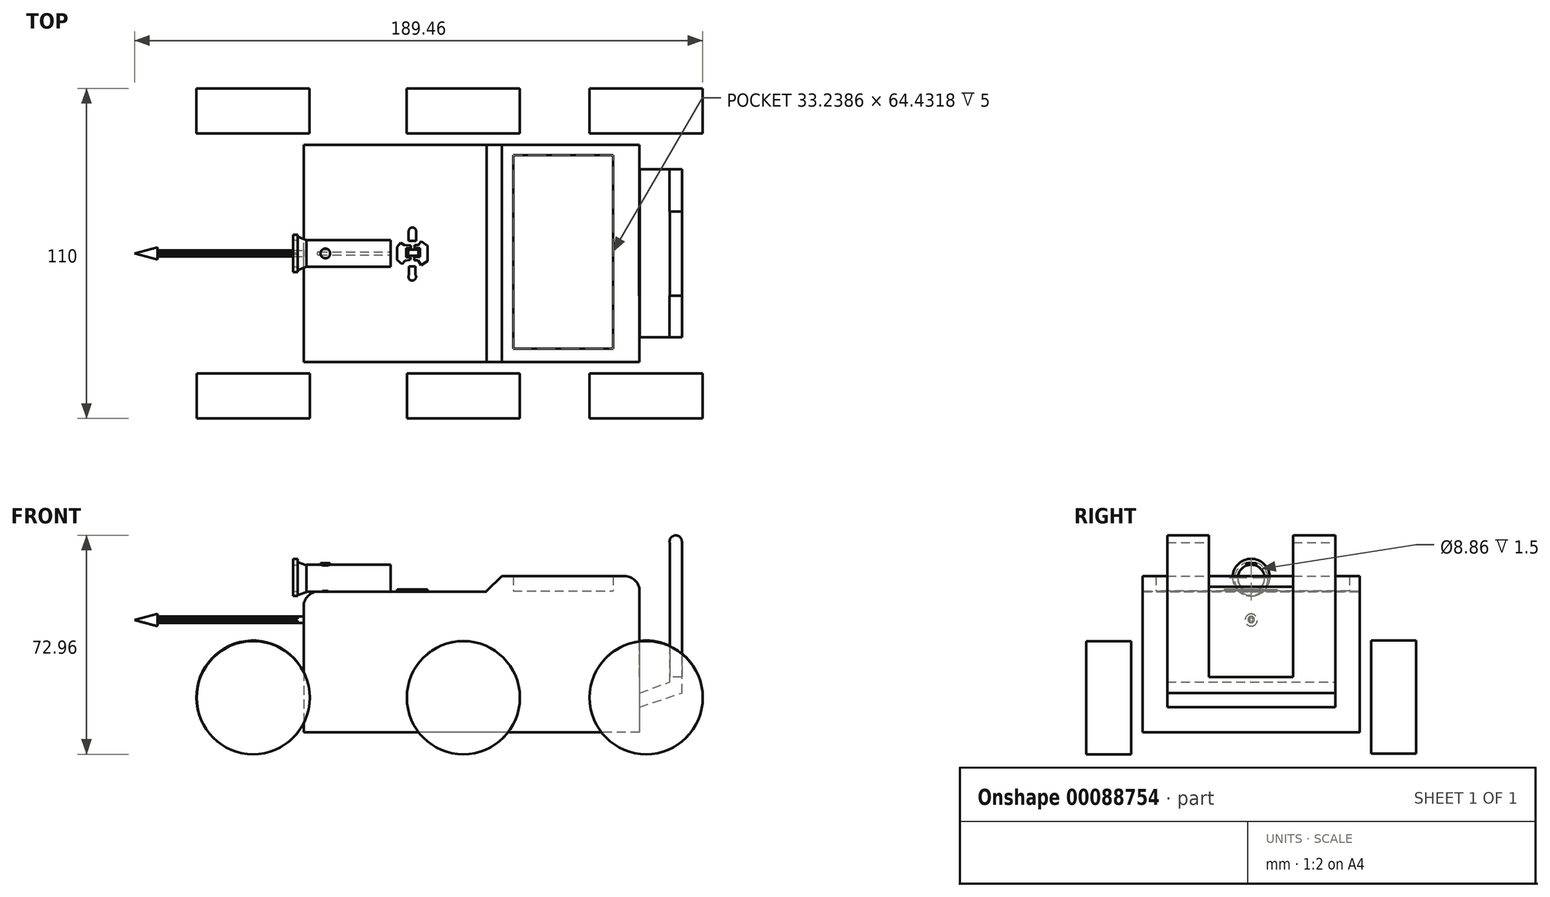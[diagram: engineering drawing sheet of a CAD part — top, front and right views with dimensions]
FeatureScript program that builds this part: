
annotation { "Feature Type Name" : "Feature", "Feature Type Description" : "" }
export const myFeature = defineFeature(function(context is Context, id is Id, definition is map)
    precondition{}
    {
        {
            var Q0;
            Q0=qCreatedBy(makeId("Front.planeOp"),FACE);
            var sketch = newSketch(context, id + "F0", { "sketchPlane" : qUnion([Q0])});
            skLineSegment(sketch, "E0.bottom", {"start": v(56, 26) * mm, "end": v(-56, 26) * mm});
            skLineSegment(sketch, "E0.top", {"start": v(56, -26) * mm, "end": v(-56, -26) * mm});
            skLineSegment(sketch, "E0.left", {"start": v(56, 26) * mm, "end": v(56, -26) * mm});
            skLineSegment(sketch, "E0.right", {"start": v(-56, 26) * mm, "end": v(-56, -26) * mm});
            skPoint(sketch, "E0.middle", {"position": v(0, 0) * mm});
            skSolve(sketch);
        }
        {
            var Q0;
            Q0=makeQuery(id+"F0.imprint","IMPRINT",FACE,{"disambiguationData":[TD([[makeQuery(id+"F0.imprint","IMPRINT",EDGE,{"derivedFrom":sQuery(id+"F0.wireOp",EDGE,"E0.bottom")}),1.0]])]});
            extrude(context, id + "F1", {"entities" : qUnion([Q0]), "depth" : 36.25 * mm, "hasSecondDirection" : true, "secondDirectionOppositeDirection" : true, "secondDirectionDepth" : 36.25 * mm});
        }
        {
            var Q0;
            Q0=qCreatedBy(makeId("Front.planeOp"),FACE);
            var sketch = newSketch(context, id + "F2", { "sketchPlane" : qUnion([Q0])});
            skLineSegment(sketch, "E1.bottom", {"start": v(-57.73, 29.14) * mm, "end": v(5.05, 29.14) * mm});
            skLineSegment(sketch, "E1.top", {"start": v(-57.73, 20.84) * mm, "end": v(5.05, 20.84) * mm});
            skLineSegment(sketch, "E1.left", {"start": v(-57.73, 29.14) * mm, "end": v(-57.73, 20.84) * mm});
            skLineSegment(sketch, "E1.right", {"start": v(5.05, 29.14) * mm, "end": v(5.05, 20.84) * mm});
            skSolve(sketch);
        }
        {
            var Q0;
            Q0 = qSketchRegion(id + "F2", true);
            var Q1;
            Q1=sQuery(id+"F2.wireOp",EDGE,"E1.bottom");
            extrude(context, id + "F3", {"entities" : qUnion([Q0]), "operationType" : NewBodyOperationType.REMOVE, "surfaceEntities" : qUnion([Q1]), "oppositeDirection" : true, "depth" : 40 * mm, "hasSecondDirection" : true, "secondDirectionOppositeDirection" : false, "secondDirectionDepth" : 40 * mm});
        }
        {
            var Q0;
            Q0=makeQuery(id+"F3.boolean.opBoolean","INTERSECT",EDGE,{"derivedFrom":[makeQuery(id+"F1.opExtrude","SWEPT_FACE",FACE,{"disambiguationData":[OSD([sQuery(id+"F0.wireOp",EDGE,"E0.bottom")])]}),makeQuery(id+"F3.opExtrude","SWEPT_FACE",FACE,{"disambiguationData":[OSD([sQuery(id+"F2.wireOp",EDGE,"E1.right")])]})]});
            chamfer(context, id + "F4", {"entities" : qUnion([Q0]), "width" : 5 * mm, "tangentPropagation" : true});
        }
        {
            var Q0;
            Q0=makeQuery(id+"F1.opExtrude","SWEPT_EDGE",EDGE,{"disambiguationData":[OSD([sQuery(id+"F0.wireOp",EDGE,"E0.bottom"),sQuery(id+"F0.wireOp",EDGE,"E0.left")])]});
            var Q1;
            Q1=makeQuery(id+"F3.boolean.opBoolean","INTERSECT",EDGE,{"derivedFrom":[makeQuery(id+"F1.opExtrude","SWEPT_FACE",FACE,{"disambiguationData":[OSD([sQuery(id+"F0.wireOp",EDGE,"E0.right")])]}),makeQuery(id+"F3.opExtrude","SWEPT_FACE",FACE,{"disambiguationData":[OSD([sQuery(id+"F2.wireOp",EDGE,"E1.top")])]})]});
            fillet(context, id + "F5", {"entities" : qUnion([Q0, Q1]), "radius" : 5 * mm, "tangentPropagation" : true, "allowEdgeOverflow" : false});
        }
        {
            var Q0;
            Q0=qCreatedBy(makeId("Top.planeOp"),FACE);
            cPlane(context, id + "F6", {"entities" : qUnion([Q0]), "cplaneType" : CPlaneType.OFFSET, "offset" : 21 * mm, "width" : 150 * mm, "height" : 150 * mm});
        }
        {
            var Q0;
            Q0=qCreatedBy(id+"F6.planeOp",FACE);
            var sketch = newSketch(context, id + "F7", { "sketchPlane" : qUnion([Q0])});
            skLineSegment(sketch, "E2", {"start": v(-14.71, 0) * mm, "end": v(-14.71, -2.5) * mm});
            skLineSegment(sketch, "E3", {"start": v(-14.71, 0) * mm, "end": v(-14.71, 2.5) * mm});
            skLineSegment(sketch, "E4", {"start": v(-14.71, 2.5) * mm, "end": v(-16.76, 4.11) * mm});
            skLineSegment(sketch, "E5", {"start": v(-16.76, 4.11) * mm, "end": v(-17.76, 2.84) * mm});
            skLineSegment(sketch, "E6", {"start": v(-17.76, 2.84) * mm, "end": v(-19.04, 2.84) * mm});
            skLineSegment(sketch, "E7", {"start": v(-19.04, 2.84) * mm, "end": v(-19.04, 1.73) * mm});
            skLineSegment(sketch, "E8", {"start": v(-19.04, 1.73) * mm, "end": v(-17.22, 1.73) * mm});
            skLineSegment(sketch, "E9", {"start": v(-17.22, 1.73) * mm, "end": v(-17.22, -1.11) * mm});
            skLineSegment(sketch, "E10", {"start": v(-17.22, -1.11) * mm, "end": v(-19.15, -1.11) * mm});
            skLineSegment(sketch, "E11", {"start": v(-19.15, -1.11) * mm, "end": v(-19.15, -2.25) * mm});
            skLineSegment(sketch, "E12", {"start": v(-19.15, -2.25) * mm, "end": v(-17.79, -2.25) * mm});
            skLineSegment(sketch, "E13", {"start": v(-17.79, -2.25) * mm, "end": v(-16.88, -3.96) * mm});
            skLineSegment(sketch, "E14", {"start": v(-16.88, -3.96) * mm, "end": v(-14.71, -2.5) * mm});
            skLineSegment(sketch, "E15", {"start": v(-20.29, 1.73) * mm, "end": v(-21.76, 1.73) * mm});
            skLineSegment(sketch, "E16", {"start": v(-21.76, 1.73) * mm, "end": v(-21.76, -1.23) * mm});
            skLineSegment(sketch, "E17", {"start": v(-21.76, -1.23) * mm, "end": v(-20.29, -1.23) * mm});
            skLineSegment(sketch, "E18", {"start": v(-20.29, -1.23) * mm, "end": v(-20.51, -2.14) * mm});
            skLineSegment(sketch, "E19", {"start": v(-20.51, -2.14) * mm, "end": v(-22.1, -2.36) * mm});
            skLineSegment(sketch, "E20", {"start": v(-22.1, -2.36) * mm, "end": v(-23.13, -3.62) * mm});
            skLineSegment(sketch, "E21", {"start": v(-23.13, -3.62) * mm, "end": v(-24.89, -2.18) * mm});
            skLineSegment(sketch, "E22", {"start": v(-24.89, -2.18) * mm, "end": v(-24.89, 2.18) * mm});
            skLineSegment(sketch, "E23", {"start": v(-24.89, 2.18) * mm, "end": v(-23.7, 3.54) * mm});
            skLineSegment(sketch, "E24", {"start": v(-23.7, 3.54) * mm, "end": v(-22.45, 2.75) * mm});
            skLineSegment(sketch, "E25", {"start": v(-22.45, 2.75) * mm, "end": v(-20.29, 2.64) * mm});
            skLineSegment(sketch, "E26", {"start": v(-20.29, 2.64) * mm, "end": v(-20.29, 1.73) * mm});
            skLineSegment(sketch, "E27", {"start": v(-18.7, -4.3) * mm, "end": v(-20.86, -4.3) * mm});
            skLineSegment(sketch, "E28", {"start": v(-18.7, -4.3) * mm, "end": v(-18.7, -7.14) * mm});
            skLineSegment(sketch, "E29", {"start": v(-20.86, -4.3) * mm, "end": v(-20.86, -7.14) * mm});
            skArc(sketch, "E30", {"start": v(-20.86, -7.14) * mm, "mid": v(-19.78, -9.06) * mm, "end": v(-18.7, -7.14) * mm});
            skLineSegment(sketch, "E31", {"start": v(-18.47, 4.23) * mm, "end": v(-20.97, 4.23) * mm});
            skLineSegment(sketch, "E32", {"start": v(-20.97, 4.23) * mm, "end": v(-20.97, 7.4) * mm});
            skLineSegment(sketch, "E33", {"start": v(-18.47, 4.23) * mm, "end": v(-18.47, 7.4) * mm});
            skArc(sketch, "E34", {"start": v(-18.47, 7.4) * mm, "mid": v(-19.72, 8.66) * mm, "end": v(-20.97, 7.4) * mm});
            skSolve(sketch);
        }
        {
            var Q0;
            Q0 = qSketchRegion(id + "F7", true);
            extrude(context, id + "F8", {"entities" : qUnion([Q0]), "depth" : 0.6 * mm});
        }
        {
            var Q0;
            Q0=qCreatedBy(id+"F6.planeOp",FACE);
            var sketch = newSketch(context, id + "F9", { "sketchPlane" : qUnion([Q0])});
            skLineSegment(sketch, "E35.bottom", {"start": v(-17.73, 1.22) * mm, "end": v(-21.1, 1.22) * mm});
            skLineSegment(sketch, "E35.top", {"start": v(-17.73, -0.79) * mm, "end": v(-21.1, -0.79) * mm});
            skLineSegment(sketch, "E35.left", {"start": v(-17.73, 1.22) * mm, "end": v(-17.73, -0.79) * mm});
            skLineSegment(sketch, "E35.right", {"start": v(-21.1, 1.22) * mm, "end": v(-21.1, -0.79) * mm});
            skSolve(sketch);
        }
        {
            var Q0;
            Q0 = qSketchRegion(id + "F9", true);
            var Q1;
            Q1 = qConstructionFilter(qBodyType(qCreatedBy(id + "F9" ,EDGE), BodyType.WIRE), ConstructionObject.NO);
            extrude(context, id + "F10", {"entities" : qUnion([Q0]), "surfaceEntities" : qUnion([Q1]), "depth" : 0.6 * mm});
        }
        {
            var Q0;
            Q0=qCreatedBy(makeId("Front.planeOp"),FACE);
            cPlane(context, id + "F11", {"entities" : qUnion([Q0]), "cplaneType" : CPlaneType.OFFSET, "offset" : 40 * mm, "width" : 150 * mm, "height" : 150 * mm});
        }
        {
            var Q0;
            Q0=qCreatedBy(id+"F11.planeOp",FACE);
            var sketch = newSketch(context, id + "F12", { "sketchPlane" : qUnion([Q0])});
            skCircle(sketch, "E36", {"center": v(-72.8, -14.52) * mm, "radius": 18.85 * mm});
            skCircle(sketch, "E37", {"center": v(-2.74, -14.52) * mm, "radius": 18.85 * mm});
            skCircle(sketch, "E38", {"center": v(58.22, -14.52) * mm, "radius": 18.85 * mm});
            skSolve(sketch);
        }
        {
            var Q0;
            Q0 = qSketchRegion(id + "F12", true);
            var Q1;
            Q1 = qConstructionFilter(qBodyType(qCreatedBy(id + "F12" ,EDGE), BodyType.WIRE), ConstructionObject.NO);
            extrude(context, id + "F13", {"entities" : qUnion([Q0]), "operationType" : NewBodyOperationType.ADD, "surfaceEntities" : qUnion([Q1]), "depth" : 15 * mm});
        }
        {
            var Q0;
            Q0=qCreatedBy(makeId("Front.planeOp"),FACE);
            cPlane(context, id + "F14", {"entities" : qUnion([Q0]), "cplaneType" : CPlaneType.OFFSET, "offset" : 36 * mm, "width" : 150 * mm, "height" : 150 * mm});
        }
        {
            var Q0;
            Q0=qCreatedBy(id+"F14.planeOp",FACE);
            var sketch = newSketch(context, id + "F15", { "sketchPlane" : qUnion([Q0])});
            skLineSegment(sketch, "E39", {"start": v(-71.34, 4.6) * mm, "end": v(-76.2, 4.6) * mm});
            skLineSegment(sketch, "E40", {"start": v(-76.2, 4.6) * mm, "end": v(-80.9, 3.16) * mm});
            skLineSegment(sketch, "E41", {"start": v(-80.9, 3.16) * mm, "end": v(-84.69, 0.81) * mm});
            skLineSegment(sketch, "E42", {"start": v(-84.69, 0.81) * mm, "end": v(-88.66, -2.8) * mm});
            skLineSegment(sketch, "E43", {"start": v(-88.66, -2.8) * mm, "end": v(-91, -7.67) * mm});
            skLineSegment(sketch, "E44", {"start": v(-91, -7.67) * mm, "end": v(-92.45, -13.08) * mm});
            skLineSegment(sketch, "E45", {"start": v(-92.45, -13.08) * mm, "end": v(-92.09, -18.5) * mm});
            skLineSegment(sketch, "E46", {"start": v(-92.09, -18.5) * mm, "end": v(-90.28, -23.72) * mm});
            skLineSegment(sketch, "E47", {"start": v(-90.28, -23.72) * mm, "end": v(-86.5, -28.6) * mm});
            skLineSegment(sketch, "E48", {"start": v(-86.5, -28.6) * mm, "end": v(-79.64, -32.93) * mm});
            skLineSegment(sketch, "E49", {"start": v(-79.64, -32.93) * mm, "end": v(-73.14, -34.55) * mm});
            skLineSegment(sketch, "E50", {"start": v(-73.14, -34.55) * mm, "end": v(-67, -33.65) * mm});
            skLineSegment(sketch, "E51", {"start": v(-67, -33.65) * mm, "end": v(-62.68, -33.65) * mm});
            skLineSegment(sketch, "E52", {"start": v(-62.68, -33.65) * mm, "end": v(-54.56, -34.19) * mm});
            skLineSegment(sketch, "E53", {"start": v(-54.56, -34.19) * mm, "end": v(-46.98, -34.37) * mm});
            skLineSegment(sketch, "E54", {"start": v(-46.98, -34.37) * mm, "end": v(-40.67, -34.9) * mm});
            skLineSegment(sketch, "E55", {"start": v(-40.67, -34.9) * mm, "end": v(-29.3, -34.9) * mm});
            skLineSegment(sketch, "E56", {"start": v(-29.3, -34.9) * mm, "end": v(-11.08, -34.9) * mm});
            skLineSegment(sketch, "E57", {"start": v(-11.08, -34.9) * mm, "end": v(0, -35.27) * mm});
            skLineSegment(sketch, "E58", {"start": v(0, -35.27) * mm, "end": v(8.58, -35.63) * mm});
            skLineSegment(sketch, "E59", {"start": v(8.58, -35.63) * mm, "end": v(15.26, -35.45) * mm});
            skLineSegment(sketch, "E60", {"start": v(15.26, -35.45) * mm, "end": v(24.28, -35.1) * mm});
            skLineSegment(sketch, "E61", {"start": v(24.28, -35.1) * mm, "end": v(34.56, -35.1) * mm});
            skLineSegment(sketch, "E62", {"start": v(34.56, -35.1) * mm, "end": v(48.1, -35.45) * mm});
            skLineSegment(sketch, "E63", {"start": v(48.1, -35.45) * mm, "end": v(60.18, -34.55) * mm});
            skLineSegment(sketch, "E64", {"start": v(60.18, -34.55) * mm, "end": v(65.78, -33.1) * mm});
            skLineSegment(sketch, "E65", {"start": v(65.78, -33.1) * mm, "end": v(70.65, -29.32) * mm});
            skLineSegment(sketch, "E66", {"start": v(70.65, -29.32) * mm, "end": v(74.98, -24.99) * mm});
            skLineSegment(sketch, "E67", {"start": v(74.98, -24.99) * mm, "end": v(77.86, -17.23) * mm});
            skLineSegment(sketch, "E68", {"start": v(77.86, -17.23) * mm, "end": v(77.86, -9.83) * mm});
            skLineSegment(sketch, "E69", {"start": v(77.86, -9.83) * mm, "end": v(75.34, -4.24) * mm});
            skLineSegment(sketch, "E70", {"start": v(75.34, -4.24) * mm, "end": v(71.9, 0) * mm});
            skLineSegment(sketch, "E71", {"start": v(71.9, 0) * mm, "end": v(67.22, 3.16) * mm});
            skLineSegment(sketch, "E72", {"start": v(67.22, 3.16) * mm, "end": v(64.15, 4.24) * mm});
            skLineSegment(sketch, "E73", {"start": v(64.15, 4.24) * mm, "end": v(60.9, 5.32) * mm});
            skLineSegment(sketch, "E74", {"start": v(60.9, 5.32) * mm, "end": v(56.93, 5.5) * mm});
            skLineSegment(sketch, "E75", {"start": v(56.93, 5.5) * mm, "end": v(50.08, 5.14) * mm});
            skLineSegment(sketch, "E76", {"start": v(50.08, 5.14) * mm, "end": v(45.93, 4.96) * mm});
            skLineSegment(sketch, "E77", {"start": v(45.93, 4.96) * mm, "end": v(40.16, 3.34) * mm});
            skLineSegment(sketch, "E78", {"start": v(40.16, 3.34) * mm, "end": v(34.38, 2.62) * mm});
            skLineSegment(sketch, "E79", {"start": v(34.38, 2.62) * mm, "end": v(27.35, 2.62) * mm});
            skLineSegment(sketch, "E80", {"start": v(27.35, 2.62) * mm, "end": v(20.5, 2.8) * mm});
            skLineSegment(sketch, "E81", {"start": v(20.5, 2.8) * mm, "end": v(14.36, 2.44) * mm});
            skLineSegment(sketch, "E82", {"start": v(14.36, 2.44) * mm, "end": v(9.49, 2.44) * mm});
            skLineSegment(sketch, "E83", {"start": v(9.49, 2.44) * mm, "end": v(4.07, 3.34) * mm});
            skLineSegment(sketch, "E84", {"start": v(4.07, 3.34) * mm, "end": v(0.29, 4.78) * mm});
            skLineSegment(sketch, "E85", {"start": v(0.29, 4.78) * mm, "end": v(-3.86, 5.14) * mm});
            skLineSegment(sketch, "E86", {"start": v(-3.86, 5.14) * mm, "end": v(-8.92, 4.42) * mm});
            skLineSegment(sketch, "E87", {"start": v(-8.92, 4.42) * mm, "end": v(-14.5, 2.07) * mm});
            skLineSegment(sketch, "E88", {"start": v(-14.5, 2.07) * mm, "end": v(-19.38, 0.63) * mm});
            skLineSegment(sketch, "E89", {"start": v(-19.38, 0.63) * mm, "end": v(-31.83, 0.1) * mm});
            skLineSegment(sketch, "E90", {"start": v(-31.83, 0.1) * mm, "end": v(-39.95, 0) * mm});
            skLineSegment(sketch, "E91", {"start": v(-39.95, 0) * mm, "end": v(-46.08, -0.1) * mm});
            skLineSegment(sketch, "E92", {"start": v(-46.08, -0.1) * mm, "end": v(-52.03, -0.1) * mm});
            skLineSegment(sketch, "E93", {"start": v(-52.03, -0.1) * mm, "end": v(-59.25, 0) * mm});
            skLineSegment(sketch, "E94", {"start": v(-59.25, 0) * mm, "end": v(-62.86, 2.07) * mm});
            skLineSegment(sketch, "E95", {"start": v(-62.86, 2.07) * mm, "end": v(-65.93, 4.06) * mm});
            skLineSegment(sketch, "E96", {"start": v(-65.93, 4.06) * mm, "end": v(-71.34, 4.6) * mm});
            skSolve(sketch);
        }
        {
            var Q0;
            Q0 = qSketchRegion(id + "F15", true);
            var Q1;
            Q1 = qConstructionFilter(qBodyType(qCreatedBy(id + "F15" ,EDGE), BodyType.WIRE), ConstructionObject.NO);
            extrude(context, id + "F16", {"entities" : qUnion([Q0]), "bodyType" : ToolBodyType.SURFACE, "surfaceEntities" : qUnion([Q1]), "depth" : 23 * mm});
        }
        {
            var Q0;
            Q0=qCreatedBy(makeId("Front.planeOp"),FACE);
            cPlane(context, id + "F17", {"entities" : qUnion([Q0]), "cplaneType" : CPlaneType.OFFSET, "offset" : 40 * mm, "oppositeDirection" : true, "width" : 150 * mm, "height" : 150 * mm});
        }
        {
            var Q0;
            Q0=qCreatedBy(makeId("Front.planeOp"),FACE);
            cPlane(context, id + "F18", {"entities" : qUnion([Q0]), "cplaneType" : CPlaneType.OFFSET, "offset" : 36 * mm, "oppositeDirection" : true, "width" : 150 * mm, "height" : 150 * mm});
        }
        {
            var Q0;
            Q0=qCreatedBy(id+"F17.planeOp",FACE);
            var sketch = newSketch(context, id + "F19", { "sketchPlane" : qUnion([Q0])});
            skCircle(sketch, "E97", {"center": v(-72.88, -14.34) * mm, "radius": 18.85 * mm});
            skCircle(sketch, "E98", {"center": v(-2.81, -14.34) * mm, "radius": 18.85 * mm});
            skCircle(sketch, "E99", {"center": v(58.14, -14.34) * mm, "radius": 18.85 * mm});
            skSolve(sketch);
        }
        {
            var Q0;
            Q0 = qSketchRegion(id + "F19", true);
            extrude(context, id + "F20", {"entities" : qUnion([Q0]), "operationType" : NewBodyOperationType.ADD, "oppositeDirection" : true, "depth" : 15 * mm});
        }
        {
            var Q0;
            Q0=qCreatedBy(id+"F18.planeOp",FACE);
            var sketch = newSketch(context, id + "F21", { "sketchPlane" : qUnion([Q0])});
            skLineSegment(sketch, "E100", {"start": v(66.5, -32.93) * mm, "end": v(70.83, -29.32) * mm});
            skLineSegment(sketch, "E101", {"start": v(70.83, -29.32) * mm, "end": v(73.9, -26.25) * mm});
            skLineSegment(sketch, "E102", {"start": v(73.9, -26.25) * mm, "end": v(75.52, -23.54) * mm});
            skLineSegment(sketch, "E103", {"start": v(75.52, -23.54) * mm, "end": v(77.32, -19.21) * mm});
            skLineSegment(sketch, "E104", {"start": v(77.32, -19.21) * mm, "end": v(78.22, -14.88) * mm});
            skLineSegment(sketch, "E105", {"start": v(78.22, -14.88) * mm, "end": v(77.86, -11.28) * mm});
            skLineSegment(sketch, "E106", {"start": v(77.86, -11.28) * mm, "end": v(75.7, -4.78) * mm});
            skLineSegment(sketch, "E107", {"start": v(75.7, -4.78) * mm, "end": v(72.81, -1.9) * mm});
            skLineSegment(sketch, "E108", {"start": v(72.81, -1.9) * mm, "end": v(69.02, 2.07) * mm});
            skLineSegment(sketch, "E109", {"start": v(69.02, 2.07) * mm, "end": v(65.23, 4.06) * mm});
            skLineSegment(sketch, "E110", {"start": v(65.23, 4.06) * mm, "end": v(60.36, 5.32) * mm});
            skLineSegment(sketch, "E111", {"start": v(60.36, 5.32) * mm, "end": v(53.69, 5.68) * mm});
            skLineSegment(sketch, "E112", {"start": v(53.69, 5.68) * mm, "end": v(45.93, 3.16) * mm});
            skLineSegment(sketch, "E113", {"start": v(45.93, 3.16) * mm, "end": v(41.96, 0.63) * mm});
            skLineSegment(sketch, "E114", {"start": v(41.96, 0.63) * mm, "end": v(35.65, -0.63) * mm});
            skLineSegment(sketch, "E115", {"start": v(35.65, -0.63) * mm, "end": v(23.92, 0.27) * mm});
            skLineSegment(sketch, "E116", {"start": v(23.92, 0.27) * mm, "end": v(20.84, 0.27) * mm});
            skLineSegment(sketch, "E117", {"start": v(20.84, 0.27) * mm, "end": v(17.06, 0.27) * mm});
            skLineSegment(sketch, "E118", {"start": v(17.06, 0.27) * mm, "end": v(13.77, 0.62) * mm});
            skLineSegment(sketch, "E119", {"start": v(13.77, 0.62) * mm, "end": v(9.91, 1.58) * mm});
            skLineSegment(sketch, "E120", {"start": v(9.91, 1.58) * mm, "end": v(5.57, 3.35) * mm});
            skLineSegment(sketch, "E121", {"start": v(5.57, 3.35) * mm, "end": v(1.63, 4.63) * mm});
            skLineSegment(sketch, "E122", {"start": v(1.63, 4.63) * mm, "end": v(-1.58, 5.2) * mm});
            skLineSegment(sketch, "E123", {"start": v(-1.58, 5.2) * mm, "end": v(-5.28, 5.36) * mm});
            skLineSegment(sketch, "E124", {"start": v(-5.28, 5.36) * mm, "end": v(-9.3, 4.47) * mm});
            skLineSegment(sketch, "E125", {"start": v(-9.3, 4.47) * mm, "end": v(-13.23, 2.79) * mm});
            skLineSegment(sketch, "E126", {"start": v(-13.23, 2.79) * mm, "end": v(-16.53, 0.53) * mm});
            skLineSegment(sketch, "E127", {"start": v(-16.53, 0.53) * mm, "end": v(-18.94, -0.83) * mm});
            skLineSegment(sketch, "E128", {"start": v(-18.94, -0.83) * mm, "end": v(-23.76, -1.31) * mm});
            skLineSegment(sketch, "E129", {"start": v(-23.76, -1.31) * mm, "end": v(-29.79, -1) * mm});
            skLineSegment(sketch, "E130", {"start": v(-29.79, -1) * mm, "end": v(-32.2, -1) * mm});
            skLineSegment(sketch, "E131", {"start": v(-32.2, -1) * mm, "end": v(-35.51, -0.85) * mm});
            skLineSegment(sketch, "E132", {"start": v(-35.51, -0.85) * mm, "end": v(-38.92, -0.85) * mm});
            skLineSegment(sketch, "E133", {"start": v(-38.92, -0.85) * mm, "end": v(-43.39, -0.6) * mm});
            skLineSegment(sketch, "E134", {"start": v(-43.39, -0.6) * mm, "end": v(-48.45, -0.51) * mm});
            skLineSegment(sketch, "E135", {"start": v(-48.45, -0.51) * mm, "end": v(-52.12, -0.51) * mm});
            skLineSegment(sketch, "E136", {"start": v(-52.12, -0.51) * mm, "end": v(-55.22, -0.17) * mm});
            skLineSegment(sketch, "E137", {"start": v(-55.22, -0.17) * mm, "end": v(-58, 0.04) * mm});
            skLineSegment(sketch, "E138", {"start": v(-58, 0.04) * mm, "end": v(-60.26, 0.67) * mm});
            skLineSegment(sketch, "E139", {"start": v(-60.26, 0.67) * mm, "end": v(-62.7, 1.8) * mm});
            skLineSegment(sketch, "E140", {"start": v(-62.7, 1.8) * mm, "end": v(-66.18, 3.7) * mm});
            skLineSegment(sketch, "E141", {"start": v(-66.18, 3.7) * mm, "end": v(-67.7, 4.31) * mm});
            skLineSegment(sketch, "E142", {"start": v(-67.7, 4.31) * mm, "end": v(-71.19, 5.15) * mm});
            skLineSegment(sketch, "E143", {"start": v(-71.19, 5.15) * mm, "end": v(-74.52, 5.07) * mm});
            skLineSegment(sketch, "E144", {"start": v(-74.52, 5.07) * mm, "end": v(-78.32, 4.16) * mm});
            skLineSegment(sketch, "E145", {"start": v(-78.32, 4.16) * mm, "end": v(-81.58, 2.8) * mm});
            skLineSegment(sketch, "E146", {"start": v(-81.58, 2.8) * mm, "end": v(-84.39, 1.13) * mm});
            skLineSegment(sketch, "E147", {"start": v(-84.39, 1.13) * mm, "end": v(-87.2, -1.45) * mm});
            skLineSegment(sketch, "E148", {"start": v(-87.2, -1.45) * mm, "end": v(-89.01, -3.35) * mm});
            skLineSegment(sketch, "E149", {"start": v(-89.01, -3.35) * mm, "end": v(-90.74, -6.47) * mm});
            skLineSegment(sketch, "E150", {"start": v(-90.74, -6.47) * mm, "end": v(-91.73, -10.26) * mm});
            skLineSegment(sketch, "E151", {"start": v(-91.73, -10.26) * mm, "end": v(-92.63, -13.6) * mm});
            skLineSegment(sketch, "E152", {"start": v(-92.63, -13.6) * mm, "end": v(-92.36, -17.66) * mm});
            skLineSegment(sketch, "E153", {"start": v(-92.36, -17.66) * mm, "end": v(-91.3, -21.53) * mm});
            skLineSegment(sketch, "E154", {"start": v(-91.3, -21.53) * mm, "end": v(-89.2, -25.54) * mm});
            skLineSegment(sketch, "E155", {"start": v(-89.2, -25.54) * mm, "end": v(-86.71, -28.98) * mm});
            skLineSegment(sketch, "E156", {"start": v(-86.71, -28.98) * mm, "end": v(-80.98, -32.23) * mm});
            skLineSegment(sketch, "E157", {"start": v(-80.98, -32.23) * mm, "end": v(-76.48, -33.85) * mm});
            skLineSegment(sketch, "E158", {"start": v(-76.48, -33.85) * mm, "end": v(-72.76, -34.52) * mm});
            skLineSegment(sketch, "E159", {"start": v(-72.76, -34.52) * mm, "end": v(-70.85, -33.95) * mm});
            skLineSegment(sketch, "E160", {"start": v(-70.85, -33.95) * mm, "end": v(-66.55, -33.85) * mm});
            skLineSegment(sketch, "E161", {"start": v(-66.55, -33.85) * mm, "end": v(-61.67, -33.66) * mm});
            skLineSegment(sketch, "E162", {"start": v(-61.67, -33.66) * mm, "end": v(-54.03, -34.05) * mm});
            skLineSegment(sketch, "E163", {"start": v(-54.03, -34.05) * mm, "end": v(-49.67, -34.05) * mm});
            skLineSegment(sketch, "E164", {"start": v(-49.67, -34.05) * mm, "end": v(-45.12, -34.83) * mm});
            skLineSegment(sketch, "E165", {"start": v(-45.12, -34.83) * mm, "end": v(-39.5, -35.14) * mm});
            skLineSegment(sketch, "E166", {"start": v(-39.5, -35.14) * mm, "end": v(-28.28, -35.29) * mm});
            skLineSegment(sketch, "E167", {"start": v(-28.28, -35.29) * mm, "end": v(-20.09, -34.98) * mm});
            skLineSegment(sketch, "E168", {"start": v(-20.09, -34.98) * mm, "end": v(-11.9, -35.14) * mm});
            skLineSegment(sketch, "E169", {"start": v(-11.9, -35.14) * mm, "end": v(-3.4, -35.44) * mm});
            skLineSegment(sketch, "E170", {"start": v(-3.4, -35.44) * mm, "end": v(4.95, -35.44) * mm});
            skLineSegment(sketch, "E171", {"start": v(4.95, -35.44) * mm, "end": v(14.05, -35.74) * mm});
            skLineSegment(sketch, "E172", {"start": v(14.05, -35.74) * mm, "end": v(21.03, -35.29) * mm});
            skLineSegment(sketch, "E173", {"start": v(21.03, -35.29) * mm, "end": v(29.22, -35.44) * mm});
            skLineSegment(sketch, "E174", {"start": v(29.22, -35.44) * mm, "end": v(39.54, -35.29) * mm});
            skLineSegment(sketch, "E175", {"start": v(39.54, -35.29) * mm, "end": v(47.58, -35.29) * mm});
            skLineSegment(sketch, "E176", {"start": v(47.58, -35.29) * mm, "end": v(56.22, -34.68) * mm});
            skLineSegment(sketch, "E177", {"start": v(56.22, -34.68) * mm, "end": v(62.6, -34.23) * mm});
            skLineSegment(sketch, "E178", {"start": v(62.6, -34.23) * mm, "end": v(66.5, -32.93) * mm});
            skSolve(sketch);
        }
        {
            var Q0;
            Q0 = qSketchRegion(id + "F21", true);
            var Q1;
            Q1 = qConstructionFilter(qBodyType(qCreatedBy(id + "F21" ,EDGE), BodyType.WIRE), ConstructionObject.NO);
            extrude(context, id + "F22", {"entities" : qUnion([Q0]), "bodyType" : ToolBodyType.SURFACE, "surfaceEntities" : qUnion([Q1]), "oppositeDirection" : true, "depth" : 23 * mm});
        }
        {
            var Q0;
            Q0=qCreatedBy(makeId("Front.planeOp"),FACE);
            var sketch = newSketch(context, id + "F23", { "sketchPlane" : qUnion([Q0])});
            skLineSegment(sketch, "E179", {"start": v(56.08, -12.94) * mm, "end": v(66.05, -9.36) * mm});
            skLineSegment(sketch, "E180", {"start": v(66.05, -9.36) * mm, "end": v(66.05, 37.17) * mm});
            skLineSegment(sketch, "E181", {"start": v(56.08, -17.64) * mm, "end": v(70.1, -12.94) * mm});
            skLineSegment(sketch, "E182", {"start": v(70.1, -12.94) * mm, "end": v(70.1, 37.54) * mm});
            skArc(sketch, "E183", {"start": v(70.1, 37.54) * mm, "mid": v(67.88, 39.58) * mm, "end": v(66.05, 37.17) * mm});
            skPoint(sketch, "E184", {"position": v(56.08, 18.4) * mm});
            skArc(sketch, "E185", {"start": v(56.08, -12.94) * mm, "mid": v(52.81, -15.3) * mm, "end": v(56.08, -17.64) * mm});
            skSolve(sketch);
        }
        {
            var Q0;
            Q0=makeQuery(id+"F23.imprint","IMPRINT",FACE,{"disambiguationData":[TD([[makeQuery(id+"F23.imprint","IMPRINT",EDGE,{"derivedFrom":sQuery(id+"F23.wireOp",EDGE,"E179")}),-1.0]])]});
            extrude(context, id + "F24", {"entities" : qUnion([Q0]), "operationType" : NewBodyOperationType.ADD, "depth" : 28 * mm, "hasSecondDirection" : true, "secondDirectionOppositeDirection" : true, "secondDirectionDepth" : 28 * mm});
        }
        {
            var Q0;
            Q0=qCreatedBy(makeId("Right.planeOp"),FACE);
            cPlane(context, id + "F25", {"entities" : qUnion([Q0]), "cplaneType" : CPlaneType.OFFSET, "offset" : 55.8 * mm, "width" : 150 * mm, "height" : 150 * mm});
        }
        {
            var Q0;
            Q0=qCreatedBy(id+"F25.planeOp",FACE);
            var sketch = newSketch(context, id + "F26", { "sketchPlane" : qUnion([Q0])});
            skLineSegment(sketch, "E186.bottom", {"start": v(-14.12, 41.34) * mm, "end": v(14.01, 41.34) * mm});
            skLineSegment(sketch, "E186.top", {"start": v(-14.12, -7.6) * mm, "end": v(14.01, -7.6) * mm});
            skLineSegment(sketch, "E186.left", {"start": v(-14.12, 41.34) * mm, "end": v(-14.12, -7.6) * mm});
            skLineSegment(sketch, "E186.right", {"start": v(14.01, 41.34) * mm, "end": v(14.01, -7.6) * mm});
            skSolve(sketch);
        }
        {
            var Q0;
            Q0 = qSketchRegion(id + "F26", true);
            extrude(context, id + "F27", {"entities" : qUnion([Q0]), "operationType" : NewBodyOperationType.REMOVE, "depth" : 25 * mm});
        }
        {
            var Q0;
            Q0=qCreatedBy(makeId("Right.planeOp"),FACE);
            cPlane(context, id + "F28", {"entities" : qUnion([Q0]), "cplaneType" : CPlaneType.OFFSET, "offset" : 27 * mm, "oppositeDirection" : true, "width" : 150 * mm, "height" : 150 * mm});
        }
        {
            var Q0;
            Q0=qCreatedBy(id+"F28.planeOp",FACE);
            var sketch = newSketch(context, id + "F29", { "sketchPlane" : qUnion([Q0])});
            skCircle(sketch, "E187", {"center": v(0, 25.31) * mm, "radius": 4.5 * mm});
            skSolve(sketch);
        }
        {
            var Q0;
            Q0 = qSketchRegion(id + "F29", true);
            extrude(context, id + "F30", {"entities" : qUnion([Q0]), "operationType" : NewBodyOperationType.ADD, "oppositeDirection" : true, "depth" : 28 * mm});
        }
        {
            var Q0;
            Q0=qCreatedBy(makeId("Right.planeOp"),FACE);
            cPlane(context, id + "F31", {"entities" : qUnion([Q0]), "cplaneType" : CPlaneType.OFFSET, "offset" : 58 * mm, "oppositeDirection" : true, "width" : 150 * mm, "height" : 150 * mm});
        }
        {
            var Q0;
            Q0=qCreatedBy(id+"F31.planeOp",FACE);
            var sketch = newSketch(context, id + "F32", { "sketchPlane" : qUnion([Q0])});
            skCircle(sketch, "E188", {"center": v(0, 25.57) * mm, "radius": 6.2 * mm});
            skSolve(sketch);
        }
        {
            var Q0;
            Q0 = qSketchRegion(id + "F32", true);
            extrude(context, id + "F33", {"entities" : qUnion([Q0]), "oppositeDirection" : true, "depth" : 1.5 * mm});
        }
        {
            var Q0;
            Q0=qCreatedBy(makeId("Front.planeOp"),FACE);
            var sketch = newSketch(context, id + "F34", { "sketchPlane" : qUnion([Q0])});
            skLineSegment(sketch, "E189", {"start": v(-55.05, 20.7) * mm, "end": v(-58.1, 19.58) * mm});
            skLineSegment(sketch, "E190", {"start": v(-58.1, 19.58) * mm, "end": v(-58.1, 25.15) * mm});
            skLineSegment(sketch, "E191", {"start": v(-58.1, 25.15) * mm, "end": v(-55.12, 25.15) * mm});
            skLineSegment(sketch, "E192", {"start": v(-55.12, 25.15) * mm, "end": v(-55.05, 20.7) * mm});
            skPoint(sketch, "E193", {"position": v(-55.12, 29.6) * mm});
            skSolve(sketch);
        }
        {
            var Q0;
            Q0=makeQuery(id+"F34.imprint","IMPRINT",FACE,{"disambiguationData":[TD([[makeQuery(id+"F34.imprint","IMPRINT",EDGE,{"derivedFrom":sQuery(id+"F34.wireOp",EDGE,"E189")}),-1.0]])]});
            var Q1;
            Q1=sQuery(id+"F34.wireOp",EDGE,"E191");
            revolve(context, id + "F35", {"entities" : qUnion([Q0]), "axis" : qUnion([Q1]), "revolveType" : RevolveType.FULL});
        }
        {
            var Q0;
            Q0=qCreatedBy(id+"F31.planeOp",FACE);
            var sketch = newSketch(context, id + "F36", { "sketchPlane" : qUnion([Q0])});
            skCircle(sketch, "E194", {"center": v(0, 25.31) * mm, "radius": 4.43 * mm});
            skSolve(sketch);
        }
        {
            var Q0;
            Q0 = qSketchRegion(id + "F36", true);
            var Q1;
            Q1=sQuery(id+"F36.wireOp",EDGE,"E194");
            extrude(context, id + "F37", {"entities" : qUnion([Q0]), "operationType" : NewBodyOperationType.REMOVE, "surfaceEntities" : qUnion([Q1]), "oppositeDirection" : true, "depth" : 25 * mm});
        }
        {
            var Q0;
            Q0=qCreatedBy(id+"F6.planeOp",FACE);
            var sketch = newSketch(context, id + "F38", { "sketchPlane" : qUnion([Q0])});
            skCircle(sketch, "E195", {"center": v(-48.75, 0) * mm, "radius": 1.62 * mm});
            skSolve(sketch);
        }
        {
            var Q0;
            Q0 = qSketchRegion(id + "F38", true);
            extrude(context, id + "F39", {"entities" : qUnion([Q0]), "operationType" : NewBodyOperationType.ADD, "depth" : 9.3 * mm});
        }
        {
            var Q0;
            Q0=qCreatedBy(id+"F6.planeOp",FACE);
            var sketch = newSketch(context, id + "F40", { "sketchPlane" : qUnion([Q0])});
            skLineSegment(sketch, "E196.bottom", {"start": v(13.9, 32.73) * mm, "end": v(47.13, 32.73) * mm});
            skLineSegment(sketch, "E196.top", {"start": v(13.9, -31.7) * mm, "end": v(47.13, -31.7) * mm});
            skLineSegment(sketch, "E196.left", {"start": v(13.9, 32.73) * mm, "end": v(13.9, -31.7) * mm});
            skLineSegment(sketch, "E196.right", {"start": v(47.13, 32.73) * mm, "end": v(47.13, -31.7) * mm});
            skSolve(sketch);
        }
        {
            var Q0;
            Q0 = qSketchRegion(id + "F40", true);
            var Q1;
            Q1=sQuery(id+"F40.wireOp",EDGE,"E196.bottom");
            extrude(context, id + "F41", {"entities" : qUnion([Q0]), "operationType" : NewBodyOperationType.REMOVE, "surfaceEntities" : qUnion([Q1]), "depth" : 25 * mm});
        }
        {
            var Q0;
            Q0=qCreatedBy(id+"F28.planeOp",FACE);
            var sketch = newSketch(context, id + "F42", { "sketchPlane" : qUnion([Q0])});
            skCircle(sketch, "E197", {"center": v(0, 11.5) * mm, "radius": 1.06 * mm});
            skSolve(sketch);
        }
        {
            var Q0;
            Q0 = qSketchRegion(id + "F42", true);
            extrude(context, id + "F43", {"entities" : qUnion([Q0]), "operationType" : NewBodyOperationType.ADD, "oppositeDirection" : true, "depth" : 80 * mm});
        }
        {
            var Q0;
            Q0=qCreatedBy(id+"F31.planeOp",FACE);
            var sketch = newSketch(context, id + "F44", { "sketchPlane" : qUnion([Q0])});
            skLineSegment(sketch, "E198", {"start": v(-0.3, 10.46) * mm, "end": v(-0.3, 11.14) * mm});
            skLineSegment(sketch, "E199", {"start": v(-0.3, 11.14) * mm, "end": v(-1.18, 11.14) * mm});
            skLineSegment(sketch, "E200", {"start": v(-1.18, 11.14) * mm, "end": v(-0.95, 10.4) * mm});
            skLineSegment(sketch, "E201", {"start": v(-0.95, 10.4) * mm, "end": v(-0.3, 10.46) * mm});
            skLineSegment(sketch, "E202", {"start": v(0.3, 11.14) * mm, "end": v(0.3, 10.46) * mm});
            skLineSegment(sketch, "E203", {"start": v(0.3, 11.14) * mm, "end": v(1.22, 11.14) * mm});
            skLineSegment(sketch, "E204", {"start": v(1.22, 11.14) * mm, "end": v(0.85, 10.36) * mm});
            skLineSegment(sketch, "E205", {"start": v(0.85, 10.36) * mm, "end": v(0.3, 10.46) * mm});
            skLineSegment(sketch, "E206", {"start": v(-0.26, 11.73) * mm, "end": v(-0.26, 12.68) * mm});
            skLineSegment(sketch, "E207", {"start": v(-0.26, 12.68) * mm, "end": v(-1.21, 12.43) * mm});
            skLineSegment(sketch, "E208", {"start": v(-1.21, 12.43) * mm, "end": v(-1.3, 12.02) * mm});
            skLineSegment(sketch, "E209", {"start": v(-1.3, 12.02) * mm, "end": v(-1.35, 11.87) * mm});
            skLineSegment(sketch, "E210", {"start": v(-1.35, 11.87) * mm, "end": v(-1.35, 11.73) * mm});
            skLineSegment(sketch, "E211", {"start": v(-1.35, 11.73) * mm, "end": v(-0.26, 11.73) * mm});
            skLineSegment(sketch, "E212", {"start": v(0.3, 12.78) * mm, "end": v(0.3, 11.75) * mm});
            skLineSegment(sketch, "E213", {"start": v(0.3, 11.75) * mm, "end": v(1.26, 11.75) * mm});
            skLineSegment(sketch, "E214", {"start": v(1.26, 11.75) * mm, "end": v(1.12, 12.78) * mm});
            skLineSegment(sketch, "E215", {"start": v(1.12, 12.78) * mm, "end": v(0.3, 12.78) * mm});
            skSolve(sketch);
        }
        {
            var Q0;
            Q0 = qSketchRegion(id + "F44", true);
            extrude(context, id + "F45", {"entities" : qUnion([Q0]), "operationType" : NewBodyOperationType.REMOVE, "oppositeDirection" : true, "depth" : 90 * mm});
        }
        {
            var Q0;
            Q0=qCreatedBy(makeId("Front.planeOp"),FACE);
            var sketch = newSketch(context, id + "F46", { "sketchPlane" : qUnion([Q0])});
            skLineSegment(sketch, "E216", {"start": v(-104.78, 11.35) * mm, "end": v(-104.78, 9.32) * mm});
            skLineSegment(sketch, "E217", {"start": v(-104.78, 9.32) * mm, "end": v(-112.39, 11.35) * mm});
            skLineSegment(sketch, "E218", {"start": v(-112.39, 11.35) * mm, "end": v(-104.78, 11.35) * mm});
            skSolve(sketch);
        }
        {
            var Q0;
            Q0 = qSketchRegion(id + "F46", true);
            var Q1;
            Q1=sQuery(id+"F46.wireOp",EDGE,"E218");
            revolve(context, id + "F47", {"operationType" : NewBodyOperationType.ADD, "entities" : qUnion([Q0]), "axis" : qUnion([Q1]), "revolveType" : RevolveType.FULL});
        }
    });
